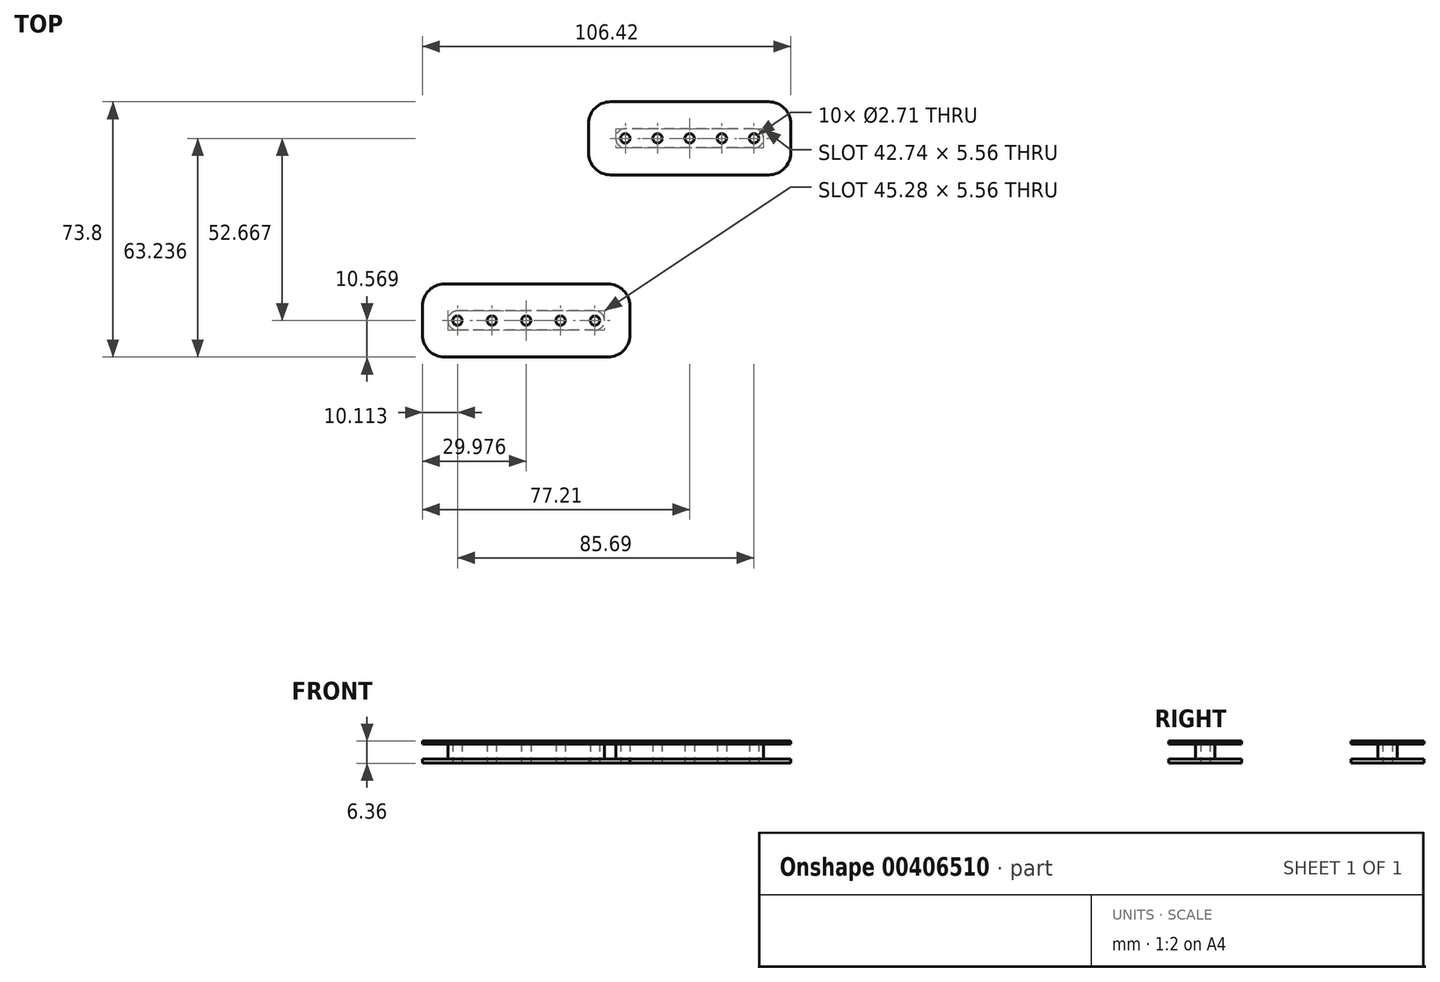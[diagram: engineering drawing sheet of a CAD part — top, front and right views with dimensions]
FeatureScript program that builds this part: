
annotation { "Feature Type Name" : "Feature", "Feature Type Description" : "" }
export const myFeature = defineFeature(function(context is Context, id is Id, definition is map)
    precondition{}
    {
        {
            var Q0;
            Q0=qCreatedBy(makeId("Top.planeOp"),FACE);
            var sketch = newSketch(context, id + "F0", { "sketchPlane" : qUnion([Q0])});
            skLineSegment(sketch, "E0.bottom", {"start": v(39.03, 27.38) * mm, "end": v(-6.69, 27.38) * mm});
            skLineSegment(sketch, "E0.top", {"start": v(39.03, 48.51) * mm, "end": v(-6.69, 48.51) * mm});
            skLineSegment(sketch, "E0.left", {"start": v(45.38, 33.73) * mm, "end": v(45.38, 42.16) * mm});
            skLineSegment(sketch, "E0.right", {"start": v(-13.04, 33.73) * mm, "end": v(-13.04, 42.16) * mm});
            skPoint(sketch, "E1.visualSharp", {"position": v(-13.04, 48.51) * mm});
            skArc(sketch, "E1.filletArc", {"start": v(-6.69, 48.51) * mm, "mid": v(-11.18, 46.65) * mm, "end": v(-13.04, 42.16) * mm});
            skPoint(sketch, "E2.visualSharp", {"position": v(-13.04, 27.38) * mm});
            skArc(sketch, "E2.filletArc", {"start": v(-13.04, 33.73) * mm, "mid": v(-11.18, 29.24) * mm, "end": v(-6.69, 27.38) * mm});
            skPoint(sketch, "E3.visualSharp", {"position": v(45.38, 27.38) * mm});
            skArc(sketch, "E3.filletArc", {"start": v(39.03, 27.38) * mm, "mid": v(43.52, 29.24) * mm, "end": v(45.38, 33.73) * mm});
            skPoint(sketch, "E4.visualSharp", {"position": v(45.38, 48.51) * mm});
            skArc(sketch, "E4.filletArc", {"start": v(45.38, 42.16) * mm, "mid": v(43.52, 46.65) * mm, "end": v(39.03, 48.51) * mm});
            skCircle(sketch, "E5", {"center": v(16.17, 37.95) * mm, "radius": 1.75 * mm, "construction": true});
            skCircle(sketch, "E6", {"center": v(6.87, 37.95) * mm, "radius": 1.75 * mm, "construction": true});
            skCircle(sketch, "E7", {"center": v(25.47, 37.95) * mm, "radius": 1.75 * mm, "construction": true});
            skCircle(sketch, "E8", {"center": v(34.76, 37.95) * mm, "radius": 1.75 * mm, "construction": true});
            skCircle(sketch, "E9", {"center": v(-2.42, 37.95) * mm, "radius": 1.75 * mm, "construction": true});
            skLineSegment(sketch, "E10", {"start": v(23.71, 37.95) * mm, "end": v(36.52, 37.95) * mm, "construction": true});
            skLineSegment(sketch, "E11", {"start": v(27.22, 37.95) * mm, "end": v(14.42, 37.95) * mm, "construction": true});
            skPoint(sketch, "E12", {"position": v(-4.18, 37.95) * mm});
            skCircle(sketch, "E13", {"center": v(-2.42, 37.95) * mm, "radius": 1.35 * mm});
            skCircle(sketch, "E14", {"center": v(6.87, 37.95) * mm, "radius": 1.35 * mm});
            skCircle(sketch, "E15", {"center": v(16.17, 37.95) * mm, "radius": 1.35 * mm});
            skCircle(sketch, "E16", {"center": v(25.47, 37.95) * mm, "radius": 1.35 * mm});
            skCircle(sketch, "E17", {"center": v(34.76, 37.95) * mm, "radius": 1.35 * mm});
            skSolve(sketch);
        }
        {
            var Q0;
            Q0=qCreatedBy(makeId("Top.planeOp"),FACE);
            var sketch = newSketch(context, id + "F1", { "sketchPlane" : qUnion([Q0])});
            skLineSegment(sketch, "E18.0", {"start": v(39.03, 27.38) * mm, "end": v(-6.69, 27.38) * mm});
            skArc(sketch, "E18.1", {"start": v(-13.04, 33.73) * mm, "mid": v(-11.18, 29.24) * mm, "end": v(-6.69, 27.38) * mm});
            skLineSegment(sketch, "E18.2", {"start": v(-13.04, 33.73) * mm, "end": v(-13.04, 42.16) * mm});
            skArc(sketch, "E18.3", {"start": v(-6.69, 48.51) * mm, "mid": v(-11.18, 46.65) * mm, "end": v(-13.04, 42.16) * mm});
            skLineSegment(sketch, "E18.4", {"start": v(39.03, 48.51) * mm, "end": v(-6.69, 48.51) * mm});
            skArc(sketch, "E18.5", {"start": v(45.38, 42.16) * mm, "mid": v(43.52, 46.65) * mm, "end": v(39.03, 48.51) * mm});
            skLineSegment(sketch, "E18.6", {"start": v(45.38, 33.73) * mm, "end": v(45.38, 42.16) * mm});
            skArc(sketch, "E18.7", {"start": v(39.03, 27.38) * mm, "mid": v(43.52, 29.24) * mm, "end": v(45.38, 33.73) * mm});
            skCircle(sketch, "E19.0", {"center": v(16.17, 37.95) * mm, "radius": 1.35 * mm, "construction": true});
            skCircle(sketch, "E19.1", {"center": v(6.87, 37.95) * mm, "radius": 1.35 * mm, "construction": true});
            skCircle(sketch, "E19.2", {"center": v(25.47, 37.95) * mm, "radius": 1.35 * mm, "construction": true});
            skCircle(sketch, "E19.3", {"center": v(34.76, 37.95) * mm, "radius": 1.35 * mm, "construction": true});
            skCircle(sketch, "E19.4", {"center": v(-2.42, 37.95) * mm, "radius": 1.35 * mm, "construction": true});
            skLineSegment(sketch, "E20.bottom", {"start": v(34.76, 40.72) * mm, "end": v(-2.42, 40.72) * mm});
            skLineSegment(sketch, "E20.top", {"start": v(34.76, 35.17) * mm, "end": v(-2.42, 35.17) * mm});
            skLineSegment(sketch, "E20.left", {"start": v(37.54, 37.95) * mm, "end": v(37.54, 37.95) * mm});
            skLineSegment(sketch, "E20.right", {"start": v(-5.2, 37.95) * mm, "end": v(-5.2, 37.95) * mm});
            skPoint(sketch, "E21.visualSharp", {"position": v(-5.2, 40.72) * mm});
            skArc(sketch, "E21.filletArc", {"start": v(-2.42, 40.72) * mm, "mid": v(-4.39, 39.9) * mm, "end": v(-5.2, 37.95) * mm});
            skPoint(sketch, "E22.visualSharp", {"position": v(-5.2, 35.17) * mm});
            skArc(sketch, "E22.filletArc", {"start": v(-5.2, 37.95) * mm, "mid": v(-4.39, 35.98) * mm, "end": v(-2.42, 35.17) * mm});
            skPoint(sketch, "E23.visualSharp", {"position": v(37.54, 35.17) * mm});
            skArc(sketch, "E23.filletArc", {"start": v(34.76, 35.17) * mm, "mid": v(36.73, 35.98) * mm, "end": v(37.54, 37.95) * mm});
            skPoint(sketch, "E24.visualSharp", {"position": v(37.54, 40.72) * mm});
            skArc(sketch, "E24.filletArc", {"start": v(37.54, 37.95) * mm, "mid": v(36.73, 39.9) * mm, "end": v(34.76, 40.72) * mm});
            skSolve(sketch);
        }
        {
            var Q0;
            Q0=qCreatedBy(makeId("Top.planeOp"),FACE);
            var sketch = newSketch(context, id + "F2", { "sketchPlane" : qUnion([Q0])});
            skLineSegment(sketch, "E25.bottom", {"start": v(-7.44, -25.29) * mm, "end": v(-54.69, -25.29) * mm});
            skLineSegment(sketch, "E25.top", {"start": v(-7.44, -4.16) * mm, "end": v(-54.69, -4.16) * mm});
            skLineSegment(sketch, "E25.left", {"start": v(-1.1, -18.94) * mm, "end": v(-1.1, -10.5) * mm});
            skLineSegment(sketch, "E25.right", {"start": v(-61.04, -18.94) * mm, "end": v(-61.04, -10.5) * mm});
            skPoint(sketch, "E26.visualSharp", {"position": v(-61.04, -4.16) * mm});
            skArc(sketch, "E26.filletArc", {"start": v(-54.69, -4.16) * mm, "mid": v(-59.18, -6.01) * mm, "end": v(-61.04, -10.5) * mm});
            skPoint(sketch, "E27.visualSharp", {"position": v(-61.04, -25.29) * mm});
            skArc(sketch, "E27.filletArc", {"start": v(-61.04, -18.94) * mm, "mid": v(-59.18, -23.43) * mm, "end": v(-54.69, -25.29) * mm});
            skPoint(sketch, "E28.visualSharp", {"position": v(-1.1, -25.29) * mm});
            skArc(sketch, "E28.filletArc", {"start": v(-7.44, -25.29) * mm, "mid": v(-2.95, -23.43) * mm, "end": v(-1.1, -18.94) * mm});
            skPoint(sketch, "E29.visualSharp", {"position": v(-1.1, -4.16) * mm});
            skArc(sketch, "E29.filletArc", {"start": v(-1.1, -10.5) * mm, "mid": v(-2.95, -6.01) * mm, "end": v(-7.44, -4.16) * mm});
            skCircle(sketch, "E30", {"center": v(-31.06, -14.72) * mm, "radius": 1.75 * mm, "construction": true});
            skCircle(sketch, "E31", {"center": v(-41, -14.72) * mm, "radius": 1.75 * mm, "construction": true});
            skCircle(sketch, "E32", {"center": v(-21.13, -14.72) * mm, "radius": 1.75 * mm, "construction": true});
            skCircle(sketch, "E33", {"center": v(-11.2, -14.72) * mm, "radius": 1.75 * mm, "construction": true});
            skCircle(sketch, "E34", {"center": v(-50.93, -14.72) * mm, "radius": 1.75 * mm, "construction": true});
            skLineSegment(sketch, "E35", {"start": v(-22.89, -14.72) * mm, "end": v(-9.45, -14.72) * mm, "construction": true});
            skLineSegment(sketch, "E36", {"start": v(-19.38, -14.72) * mm, "end": v(-32.82, -14.72) * mm, "construction": true});
            skPoint(sketch, "E37", {"position": v(-52.68, -14.72) * mm});
            skCircle(sketch, "E38", {"center": v(-50.93, -14.72) * mm, "radius": 1.35 * mm});
            skCircle(sketch, "E39", {"center": v(-41, -14.72) * mm, "radius": 1.35 * mm});
            skCircle(sketch, "E40", {"center": v(-31.06, -14.72) * mm, "radius": 1.35 * mm});
            skCircle(sketch, "E41", {"center": v(-21.13, -14.72) * mm, "radius": 1.35 * mm});
            skCircle(sketch, "E42", {"center": v(-11.2, -14.72) * mm, "radius": 1.35 * mm});
            skSolve(sketch);
        }
        {
            var Q0;
            Q0=qCreatedBy(makeId("Top.planeOp"),FACE);
            var sketch = newSketch(context, id + "F3", { "sketchPlane" : qUnion([Q0])});
            skLineSegment(sketch, "E43.0", {"start": v(-7.44, -4.16) * mm, "end": v(-54.69, -4.16) * mm});
            skArc(sketch, "E44.0", {"start": v(-54.69, -4.16) * mm, "mid": v(-59.18, -6.01) * mm, "end": v(-61.04, -10.5) * mm});
            skLineSegment(sketch, "E45.0", {"start": v(-61.04, -18.94) * mm, "end": v(-61.04, -10.5) * mm});
            skArc(sketch, "E46.0", {"start": v(-61.04, -18.94) * mm, "mid": v(-59.18, -23.43) * mm, "end": v(-54.69, -25.29) * mm});
            skLineSegment(sketch, "E47.0", {"start": v(-7.44, -25.29) * mm, "end": v(-54.69, -25.29) * mm});
            skArc(sketch, "E48.0", {"start": v(-7.44, -25.29) * mm, "mid": v(-2.95, -23.43) * mm, "end": v(-1.1, -18.94) * mm});
            skLineSegment(sketch, "E49.0", {"start": v(-1.1, -18.94) * mm, "end": v(-1.1, -10.5) * mm});
            skArc(sketch, "E50.0", {"start": v(-1.1, -10.5) * mm, "mid": v(-2.95, -6.01) * mm, "end": v(-7.44, -4.16) * mm});
            skCircle(sketch, "E51.0", {"center": v(-50.93, -14.72) * mm, "radius": 1.35 * mm, "construction": true});
            skCircle(sketch, "E52.0", {"center": v(-41, -14.72) * mm, "radius": 1.35 * mm, "construction": true});
            skCircle(sketch, "E53.0", {"center": v(-31.06, -14.72) * mm, "radius": 1.35 * mm, "construction": true});
            skCircle(sketch, "E54.0", {"center": v(-21.13, -14.72) * mm, "radius": 1.35 * mm, "construction": true});
            skCircle(sketch, "E55.0", {"center": v(-11.2, -14.72) * mm, "radius": 1.35 * mm, "construction": true});
            skLineSegment(sketch, "E56.bottom", {"start": v(-11.2, -17.5) * mm, "end": v(-50.93, -17.5) * mm});
            skLineSegment(sketch, "E56.top", {"start": v(-11.2, -11.94) * mm, "end": v(-50.93, -11.94) * mm});
            skLineSegment(sketch, "E56.left", {"start": v(-8.42, -14.72) * mm, "end": v(-8.42, -14.72) * mm});
            skLineSegment(sketch, "E56.right", {"start": v(-53.7, -14.72) * mm, "end": v(-53.7, -14.72) * mm});
            skPoint(sketch, "E57.visualSharp", {"position": v(-53.7, -11.94) * mm});
            skArc(sketch, "E57.filletArc", {"start": v(-50.93, -11.94) * mm, "mid": v(-52.9, -12.76) * mm, "end": v(-53.7, -14.72) * mm});
            skPoint(sketch, "E58.visualSharp", {"position": v(-53.7, -17.5) * mm});
            skArc(sketch, "E58.filletArc", {"start": v(-53.7, -14.72) * mm, "mid": v(-52.9, -16.69) * mm, "end": v(-50.93, -17.5) * mm});
            skPoint(sketch, "E59.visualSharp", {"position": v(-8.42, -17.5) * mm});
            skArc(sketch, "E59.filletArc", {"start": v(-11.2, -17.5) * mm, "mid": v(-9.24, -16.69) * mm, "end": v(-8.42, -14.72) * mm});
            skPoint(sketch, "E60.visualSharp", {"position": v(-8.42, -11.94) * mm});
            skArc(sketch, "E60.filletArc", {"start": v(-8.42, -14.72) * mm, "mid": v(-9.24, -12.76) * mm, "end": v(-11.2, -11.94) * mm});
            skSolve(sketch);
        }
        {
            var Q0;
            Q0 = qSketchRegion(id + "F0", true);
            var Q1;
            Q1 = qSketchRegion(id + "F2", true);
            extrude(context, id + "F4", {"entities" : qUnion([Q0, Q1]), "endBound" : BoundingType.SYMMETRIC, "depth" : 6.35 * mm, "offsetDistance" : 25.4 * mm});
        }
        {
            var Q0;
            Q0 = qSketchRegion(id + "F1", true);
            var Q1;
            Q1 = qSketchRegion(id + "F3", true);
            var Q2;
            Q2 = qConstructionFilter(qBodyType(qCreatedBy(id + "F1" ,EDGE), BodyType.WIRE), ConstructionObject.NO);
            extrude(context, id + "F5", {"entities" : qUnion([Q0, Q1]), "operationType" : NewBodyOperationType.REMOVE, "surfaceEntities" : qUnion([Q2]), "depth" : 2.38 * mm, "offsetDistance" : 25.4 * mm, "hasSecondDirection" : true, "secondDirectionOppositeDirection" : true, "secondDirectionDepth" : 1.98 * mm});
        }
    });
